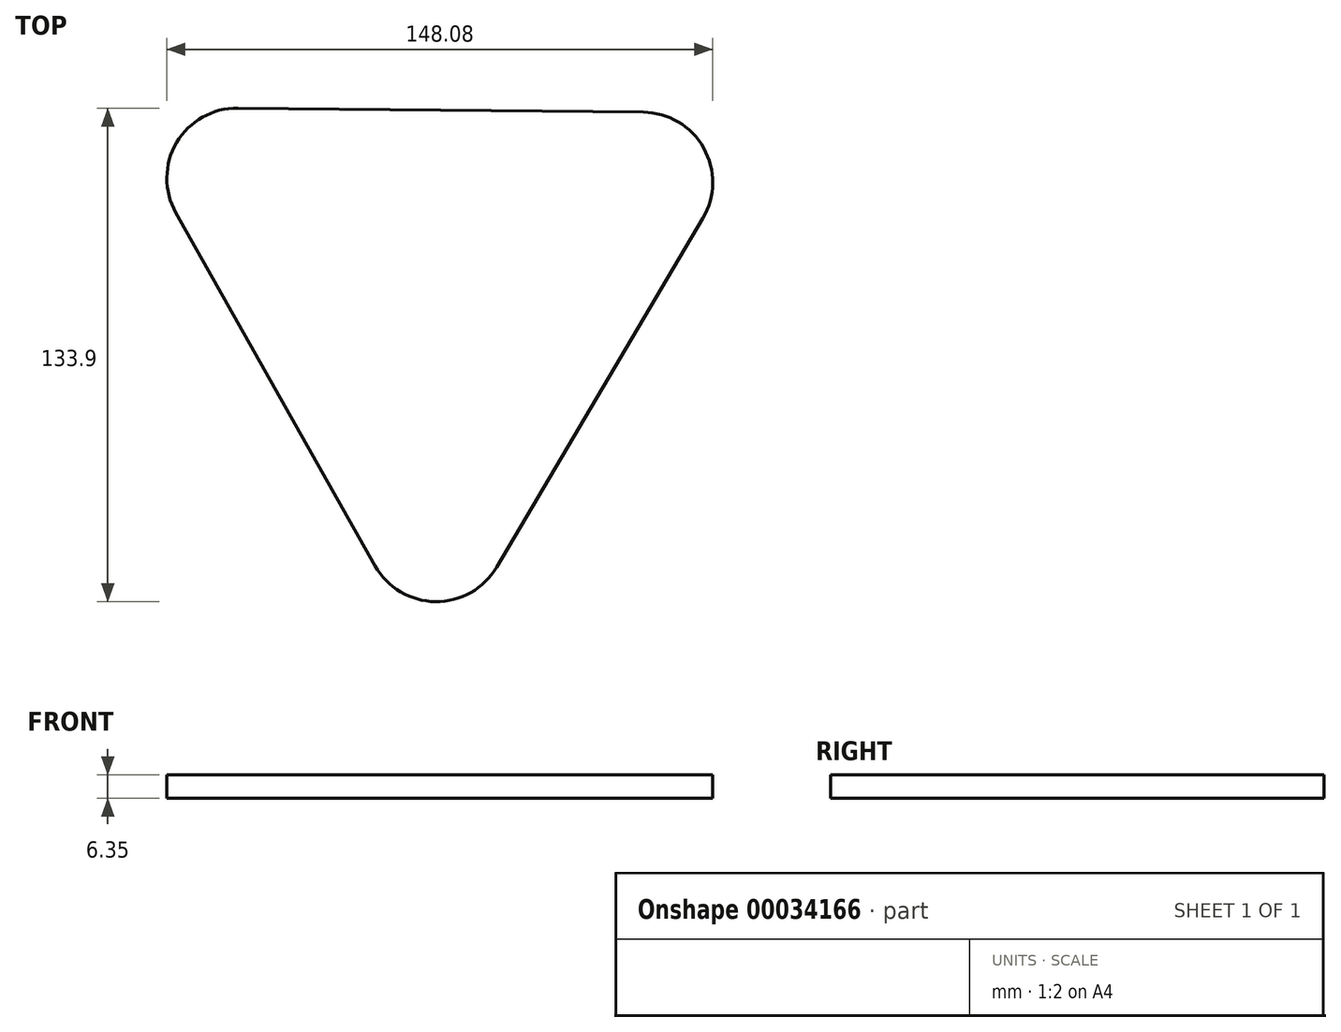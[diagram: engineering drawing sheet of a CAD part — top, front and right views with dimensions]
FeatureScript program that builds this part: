
annotation { "Feature Type Name" : "Feature", "Feature Type Description" : "" }
export const myFeature = defineFeature(function(context is Context, id is Id, definition is map)
    precondition{}
    {
        {
            var Q0;
            Q0=qCreatedBy(makeId("Top.planeOp"),FACE);
            var sketch = newSketch(context, id + "F0", { "sketchPlane" : qUnion([Q0])});
            skCircle(sketch, "E0.cCircle", {"center": v(0, 0) * mm, "radius": 101.6 * mm, "construction": true});
            skLineSegment(sketch, "E0.0", {"start": v(71.71, 21.5) * mm, "end": v(15.76, -73.19) * mm});
            skLineSegment(sketch, "E0.1", {"start": v(-17.23, -72.86) * mm, "end": v(-71.26, 22.94) * mm});
            skLineSegment(sketch, "E0.2", {"start": v(-54.48, 51.35) * mm, "end": v(55.5, 50.24) * mm});
            skPoint(sketch, "E1.visualSharp", {"position": v(-87.47, 51.68) * mm});
            skArc(sketch, "E1.filletArc", {"start": v(-54.48, 51.35) * mm, "mid": v(-71.07, 42) * mm, "end": v(-71.26, 22.94) * mm});
            skPoint(sketch, "E2.visualSharp", {"position": v(88.5, 49.91) * mm});
            skArc(sketch, "E2.filletArc", {"start": v(71.71, 21.5) * mm, "mid": v(71.9, 40.55) * mm, "end": v(55.5, 50.24) * mm});
            skPoint(sketch, "E3.visualSharp", {"position": v(-1.02, -101.6) * mm});
            skArc(sketch, "E3.filletArc", {"start": v(-17.23, -72.86) * mm, "mid": v(-0.83, -82.55) * mm, "end": v(15.76, -73.19) * mm});
            skSolve(sketch);
        }
        {
            var Q0;
            Q0 = qSketchRegion(id + "F0", true);
            extrude(context, id + "F1", {"entities" : qUnion([Q0]), "depth" : 6.35 * mm});
        }
    });
